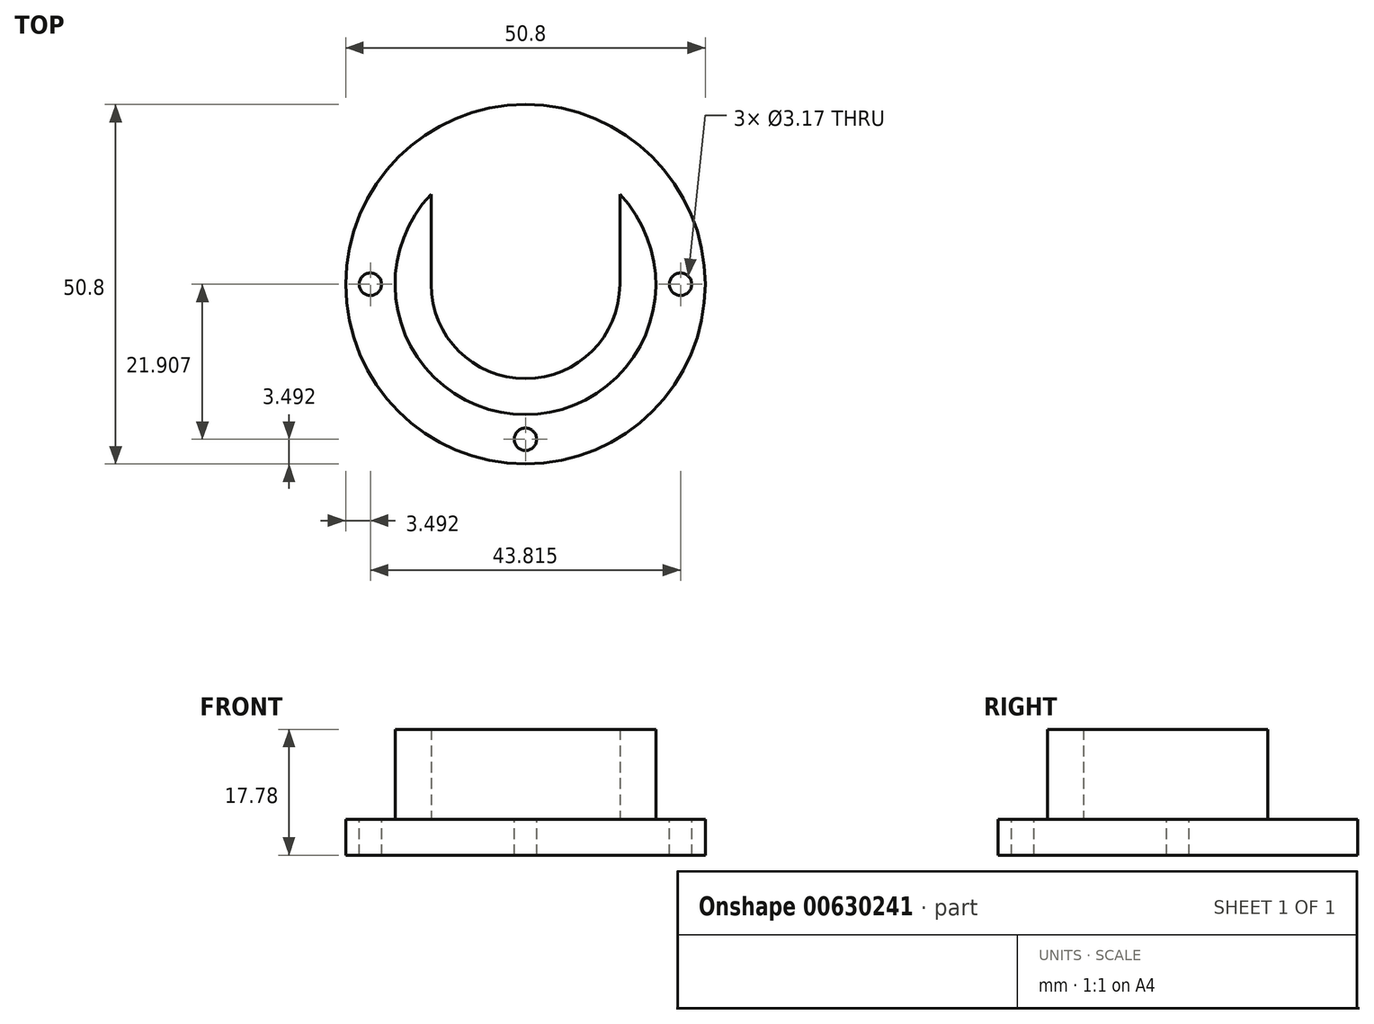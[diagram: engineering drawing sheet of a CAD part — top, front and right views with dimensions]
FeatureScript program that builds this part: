
annotation { "Feature Type Name" : "Feature", "Feature Type Description" : "" }
export const myFeature = defineFeature(function(context is Context, id is Id, definition is map)
    precondition{}
    {
        {
            var Q0;
            Q0=qCreatedBy(makeId("Top.planeOp"),FACE);
            var sketch = newSketch(context, id + "F0", { "sketchPlane" : qUnion([Q0])});
            skCircle(sketch, "E0", {"center": v(0, 0) * mm, "radius": 25.4 * mm});
            skSolve(sketch);
        }
        {
            var Q0;
            Q0=makeQuery(id+"F0.imprint","IMPRINT",FACE,{"disambiguationData":[TD([[makeQuery(id+"F0.imprint","IMPRINT",EDGE,{"derivedFrom":sQuery(id+"F0.wireOp",EDGE,"E0")}),1.0]])]});
            extrude(context, id + "F1", {"entities" : qUnion([Q0]), "depth" : 5.08 * mm, "offsetDistance" : 25.4 * mm});
        }
        {
            var Q0;
            Q0=makeQuery(id+"F1.opExtrude","CAP_FACE",FACE,{"disambiguationData":[OSD([sQuery(id+"F0.wireOp",EDGE,"E0")])],"isStart":false});
            var sketch = newSketch(context, id + "F2", { "sketchPlane" : qUnion([Q0])});
            skArc(sketch, "E1", {"start": v(-13.34, 0) * mm, "mid": v(0, -13.34) * mm, "end": v(13.34, 0) * mm});
            skArc(sketch, "E2", {"start": v(-13.34, 12.7) * mm, "mid": v(0, -18.41) * mm, "end": v(13.33, 12.7) * mm});
            skLineSegment(sketch, "E3.left", {"start": v(-13.34, 0) * mm, "end": v(-13.34, 12.7) * mm});
            skLineSegment(sketch, "E3.right", {"start": v(13.33, 0) * mm, "end": v(13.33, 12.7) * mm});
            skSolve(sketch);
        }
        {
            var Q0;
            Q0=makeQuery(id+"F2.imprint","IMPRINT",FACE,{"disambiguationData":[TD([[makeQuery(id+"F2.imprint","IMPRINT",EDGE,{"derivedFrom":sQuery(id+"F2.wireOp",EDGE,"E1")}),-1.0]])]});
            extrude(context, id + "F3", {"entities" : qUnion([Q0]), "operationType" : NewBodyOperationType.ADD, "depth" : 12.7 * mm, "offsetDistance" : 25.4 * mm});
        }
        {
            var Q0;
            Q0=makeQuery(id+"F1.opExtrude","CAP_FACE",FACE,{"disambiguationData":[OSD([sQuery(id+"F0.wireOp",EDGE,"E0")])],"isStart":false});
            var sketch = newSketch(context, id + "F4", { "sketchPlane" : qUnion([Q0])});
            skCircle(sketch, "E4", {"center": v(-21.9, 0) * mm, "radius": 1.59 * mm});
            skCircle(sketch, "E5", {"center": v(21.9, 0) * mm, "radius": 1.59 * mm});
            skCircle(sketch, "E6", {"center": v(0, -21.9) * mm, "radius": 1.59 * mm});
            skSolve(sketch);
        }
        {
            var Q0;
            Q0 = qSketchRegion(id + "F4", true);
            extrude(context, id + "F5", {"entities" : qUnion([Q0]), "operationType" : NewBodyOperationType.REMOVE, "oppositeDirection" : true, "depth" : 25.4 * mm, "offsetDistance" : 25.4 * mm});
        }
    });
